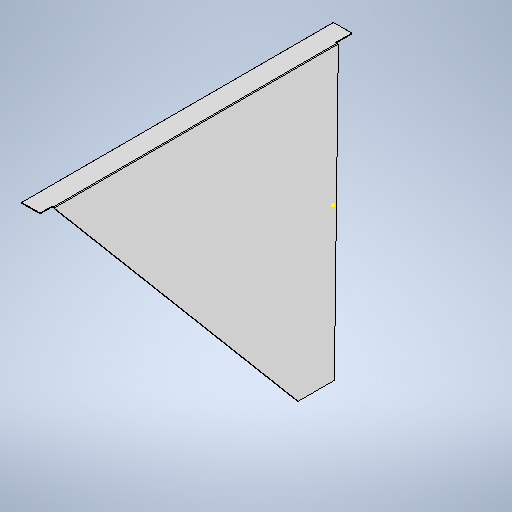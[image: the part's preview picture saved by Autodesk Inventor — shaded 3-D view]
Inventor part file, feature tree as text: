
AUTODESK INVENTOR PART (.ipt)
format: ipt  version: 2025 (Build 290162010, 162A)  size: 351,232 bytes
history: native  units: mm
features: sketch x4, sheet_metal_op x3, other x3, extrude x2
ambient origin geometry x8: Origin, YZ Plane, XZ Plane, XY Plane, X Axis, Y Axis, Z Axis, Center Point
bodies: Solid1 (feature_tree)
feature tree (12):
  sheet_metal_op  "Contour Flange1"
  extrude  "Extrusion6"  Depth=4.0mm
  extrude  "Extrusion7"  Depth=2.0mm
  other  "A-Side Definition"
  sketch  "Sketch16"  dims[d11=1536.0mm d12=6.0mm d13=4.0mm d14=16.0mm d15=4.0mm d16=6.0mm d61=88.0mm d62=230.0mm d63=1150.0mm d64=6.0mm d65=800.0mm d66=60.0mm d68=10.0mm d69=0.0mm d71=4.0mm d72=0.0mm d90=50.0mm d93=196.0mm d94=66.0mm d95=6.0mm d96=87.0mm d97=3.0mm]
  sketch  "Sketch1"  dims[d6=4.0mm d7=4.0mm]
  other  "Plate1"
  sheet_metal_op  "Bend1"
  sheet_metal_op  "Corner1"
  sketch  "Sketch9"  dims[d8=2.0mm d9=8.0mm]
  sketch  "Sketch10"  dims[d10=6.0mm]
  other  "Definition1"
